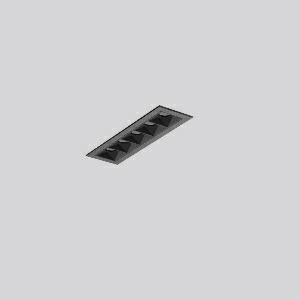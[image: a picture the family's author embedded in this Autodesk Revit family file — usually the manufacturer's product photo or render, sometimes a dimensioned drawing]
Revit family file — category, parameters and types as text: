
# Revit family: beamline_slim_641325_003_69dd
name_source: partatom
category: Lighting Fixtures
units: mm (PartAtom-declared; Revit-internal decimal feet)

## family parameters
Cut with Voids When Loaded = No
Host = Face
Light Source = No
Part Type = Normal
Room Calculation Point = No
Round Connector Dimension = Use Diameter
Shared = No

## types (1)
- BEAMLINE SLIM (1 x LED Modul 927, 960 lm, 2700)
    Apparent Load = 14 VA
    CIE Flux Codes = 100 100 100 100 100
    Color Rendering = 92
    Color Temperature = 2700
    Default Elevation = 1800 mm
    Description = Series: BEAMLINE SLIM
Minimalistic recessed ceiling luminaire for aesthetically sophisticated lighting. Housing: metal, powder-coated. Perfect heat management with an aluminium heat sink. LED light unit with MRS technology: Mini-Reflector-System made of metallised thermoplastic with prismatic black glare-suppressing frame for pleasant glare-free light (RUG < 10). Wide beam light distribution. Ceiling installation with spring system. Including separate LED converter with connecting cable 450 mm. 
Colour: deep black, matt (RAL 9005)
Length: 155 mm
Width: 45 mm
Height: 1.5 mm
Cut-out length: 150 mm
Cut-out width: 40 mm
Recess height: 110 mm
Luminaire: recess height: 60 mm
Lamp: LED
Socket: without socket
Colour temperature: 2700K
Colour rendering index (CRI): 90
System power: 14 W
Rated luminous flux: 960 lm
Luminous efficiency: 69 lm/W
Control gear: Regulated power supply
Protection class: II
Type of protection: IP 20
    Height = 0 mm  [stored 0 ft]
    Lamp = 1 x LED Modul 927
    Lamp Light Flux = 960 lm
    Lamp count = 1
    Length = 155 mm
    Lifetime = 50000 h
    Luminous efficacy = 69 lm/W
    Manufacturer = RZB
    ModVariant = No
    Model = 641325.003
    Mounting Place = Ceiling
    Mounting Type = Recessed
    Number of Poles = 1
    OnlyDefault = Yes
    Power Factor = 1
    Product Name = BEAMLINE SLIM
    Product group = Recessed LED linear luminaires
    ProductGroupID = 407
    Protection Class = Protection class II
    Protection Degree = IP 20
    RLX_Detail_Level = 1
    RLX_Emergency_Light_Flux = 0 lm
    RLX_Emergency_Type = 0
    RLX_Emergency_Type_DB = No
    RlxData = <blob elided: 12053 chars, md5=28d63fe0>
    Socket = socket
    Standby Power = 0 W
    System Light Flux = 960 lm
    System Power = 14 W
    Type Comments = Product without accessories
    Type Image = 641323.003.jpg
    URL = http://relux.com
    VarID = ---
    Voltage = 230 V
    Voltage Range = 220-240 V
    Weight = 0.00 kg
    Width = 45 mm

note: [stored X ft] marks values corroborated as IEEE doubles in the binary element streams (Revit-internal decimal feet)

## geometry (parser evidence)
native form markers: Sweep x10
no freeform markers — native parametric forms only
